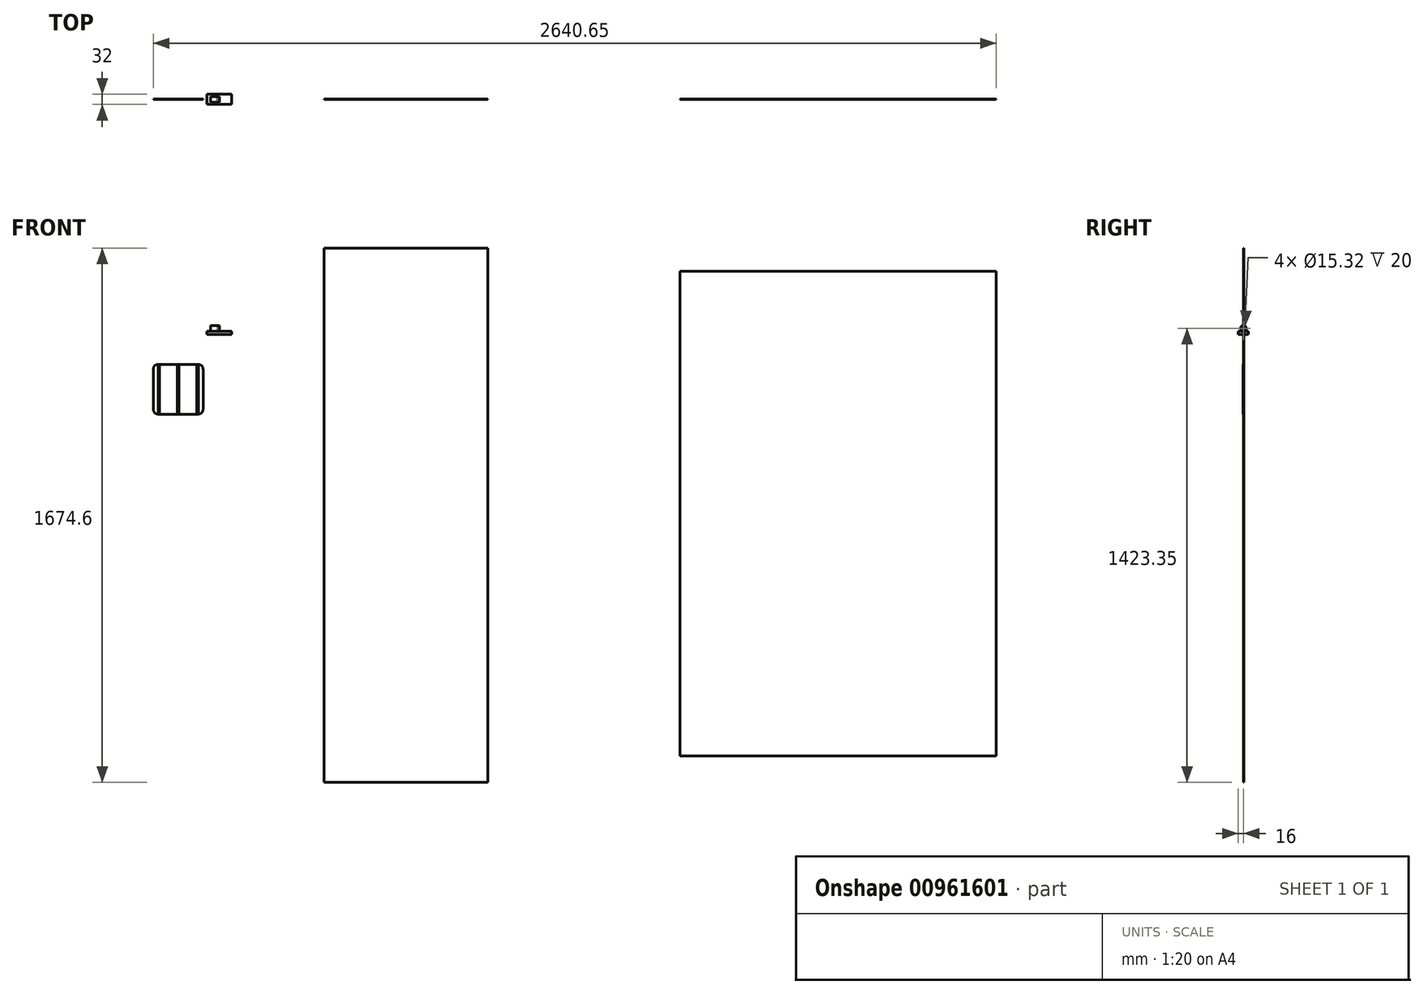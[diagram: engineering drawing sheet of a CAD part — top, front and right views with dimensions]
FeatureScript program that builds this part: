
annotation { "Feature Type Name" : "Feature", "Feature Type Description" : "" }
export const myFeature = defineFeature(function(context is Context, id is Id, definition is map)
    precondition{}
    {
        {
            var Q0;
            Q0=qCreatedBy(makeId("Front.planeOp"),FACE);
            var sketch = newSketch(context, id + "F0", { "sketchPlane" : qUnion([Q0])});
            skLineSegment(sketch, "E0", {"start": v(1286.74, 1046.2) * mm, "end": v(1798.74, 1046.2) * mm});
            skLineSegment(sketch, "E1", {"start": v(1798.74, -628.4) * mm, "end": v(1286.74, -628.4) * mm});
            skLineSegment(sketch, "E2", {"start": v(1286.74, 1046.2) * mm, "end": v(1286.74, -628.4) * mm});
            skLineSegment(sketch, "E3", {"start": v(1798.74, 1046.2) * mm, "end": v(1798.74, -628.4) * mm});
            skSolve(sketch);
        }
        {
            var Q0;
            Q0=makeQuery(id+"F0.imprint","IMPRINT",FACE,{"disambiguationData":[TD([[makeQuery(id+"F0.imprint","IMPRINT",EDGE,{"derivedFrom":sQuery(id+"F0.wireOp",EDGE,"E0")}),-1.0]])]});
            var sketch = newSketch(context, id + "F1", { "sketchPlane" : qUnion([Q0])});
            skLineSegment(sketch, "E4.bottom", {"start": v(766.3, 681.77) * mm, "end": v(892.3, 681.77) * mm});
            skLineSegment(sketch, "E4.top", {"start": v(766.3, 525.77) * mm, "end": v(892.3, 525.77) * mm});
            skLineSegment(sketch, "E4.left", {"start": v(751.3, 666.77) * mm, "end": v(751.3, 540.77) * mm});
            skLineSegment(sketch, "E4.right", {"start": v(907.3, 666.77) * mm, "end": v(907.3, 540.77) * mm});
            skPoint(sketch, "E5.visualSharp", {"position": v(751.3, 681.77) * mm});
            skArc(sketch, "E5.filletArc", {"start": v(766.3, 681.77) * mm, "mid": v(755.7, 677.38) * mm, "end": v(751.3, 666.77) * mm});
            skPoint(sketch, "E6.visualSharp", {"position": v(907.3, 681.77) * mm});
            skArc(sketch, "E6.filletArc", {"start": v(907.3, 666.77) * mm, "mid": v(902.9, 677.38) * mm, "end": v(892.3, 681.77) * mm});
            skPoint(sketch, "E7.visualSharp", {"position": v(907.3, 525.77) * mm});
            skArc(sketch, "E7.filletArc", {"start": v(892.3, 525.77) * mm, "mid": v(902.9, 530.16) * mm, "end": v(907.3, 540.77) * mm});
            skPoint(sketch, "E8.visualSharp", {"position": v(751.3, 525.77) * mm});
            skArc(sketch, "E8.filletArc", {"start": v(751.3, 540.77) * mm, "mid": v(755.7, 530.16) * mm, "end": v(766.3, 525.77) * mm});
            skLineSegment(sketch, "E9.bottom", {"start": v(3038.85, 81858.35) * mm, "end": v(2869.38, 81858.35) * mm});
            skLineSegment(sketch, "E9.top", {"start": v(3038.85, 72650.5) * mm, "end": v(2869.38, 72650.5) * mm});
            skLineSegment(sketch, "E9.left", {"start": v(3038.85, 81858.35) * mm, "end": v(3038.85, 72650.5) * mm});
            skLineSegment(sketch, "E9.right", {"start": v(2869.38, 81858.35) * mm, "end": v(2869.38, 72650.5) * mm});
            skSolve(sketch);
        }
        {
            var Q0;
            Q0=makeQuery(id+"F0.imprint","IMPRINT",FACE,{"disambiguationData":[TD([[makeQuery(id+"F0.imprint","IMPRINT",EDGE,{"derivedFrom":sQuery(id+"F0.wireOp",EDGE,"E0")}),-1.0]])]});
            extrude(context, id + "F2", {"entities" : qUnion([Q0]), "depth" : 1 * mm, "offsetDistance" : 25 * mm});
        }
        {
            var Q0;
            Q0=makeQuery(id+"F1.imprint","IMPRINT",FACE,{"disambiguationData":[TD([[makeQuery(id+"F1.imprint","IMPRINT",EDGE,{"derivedFrom":sQuery(id+"F1.wireOp",EDGE,"E4.bottom")}),-1.0]])]});
            extrude(context, id + "F3", {"entities" : qUnion([Q0]), "depth" : 1 * mm, "offsetDistance" : 25 * mm});
        }
        {
            var Q0;
            Q0=makeQuery(id+"F3.opExtrude","CAP_FACE",FACE,{"disambiguationData":[OSD([sQuery(id+"F1.wireOp",EDGE,"E4.bottom"),sQuery(id+"F1.wireOp",EDGE,"E4.top"),sQuery(id+"F1.wireOp",EDGE,"E4.left"),sQuery(id+"F1.wireOp",EDGE,"E4.right"),sQuery(id+"F1.wireOp",EDGE,"E5.filletArc"),sQuery(id+"F1.wireOp",EDGE,"E6.filletArc"),sQuery(id+"F1.wireOp",EDGE,"E7.filletArc"),sQuery(id+"F1.wireOp",EDGE,"E8.filletArc")])],"isStart":false});
            var sketch = newSketch(context, id + "F4", { "sketchPlane" : qUnion([Q0])});
            skLineSegment(sketch, "E10.bottom", {"start": v(1068.35, 691.33) * mm, "end": v(1072.64, 691.33) * mm});
            skLineSegment(sketch, "E10.top", {"start": v(1068.35, 535.33) * mm, "end": v(1072.64, 535.33) * mm});
            skLineSegment(sketch, "E10.left", {"start": v(1068.35, 691.33) * mm, "end": v(1068.35, 535.33) * mm});
            skLineSegment(sketch, "E10.right", {"start": v(1072.64, 691.33) * mm, "end": v(1072.64, 535.33) * mm});
            skLineSegment(sketch, "E11.bottom", {"start": v(1040.3, 699.13) * mm, "end": v(1044.6, 699.13) * mm});
            skLineSegment(sketch, "E11.top", {"start": v(1040.3, 543.13) * mm, "end": v(1044.6, 543.13) * mm});
            skLineSegment(sketch, "E11.left", {"start": v(1040.3, 699.13) * mm, "end": v(1040.3, 543.13) * mm});
            skLineSegment(sketch, "E11.right", {"start": v(1044.6, 699.13) * mm, "end": v(1044.6, 543.13) * mm});
            skLineSegment(sketch, "E12.bottom", {"start": v(997.94, 678.37) * mm, "end": v(1002.23, 678.37) * mm});
            skLineSegment(sketch, "E12.top", {"start": v(997.94, 522.37) * mm, "end": v(1002.23, 522.37) * mm});
            skLineSegment(sketch, "E12.left", {"start": v(997.94, 678.37) * mm, "end": v(997.94, 522.37) * mm});
            skLineSegment(sketch, "E12.right", {"start": v(1002.23, 678.37) * mm, "end": v(1002.23, 522.37) * mm});
            skSolve(sketch);
        }
        {
            var Q0;
            Q0=makeQuery(id+"F4.imprint","IMPRINT",FACE,{"disambiguationData":[TD([[makeQuery(id+"F4.imprint","IMPRINT",EDGE,{"derivedFrom":sQuery(id+"F4.wireOp",EDGE,"E10.bottom")}),-1.0]])]});
            var Q1;
            Q1=makeQuery(id+"F4.imprint","IMPRINT",FACE,{"disambiguationData":[TD([[makeQuery(id+"F4.imprint","IMPRINT",EDGE,{"derivedFrom":sQuery(id+"F4.wireOp",EDGE,"E11.bottom")}),-1.0]])]});
            var Q2;
            Q2=makeQuery(id+"F4.imprint","IMPRINT",FACE,{"disambiguationData":[TD([[makeQuery(id+"F4.imprint","IMPRINT",EDGE,{"derivedFrom":sQuery(id+"F4.wireOp",EDGE,"E12.bottom")}),-1.0]])]});
            extrude(context, id + "F5", {"entities" : qUnion([Q0, Q1, Q2]), "depth" : 0.5 * mm, "offsetDistance" : 25 * mm});
        }
        {
            var Q0;
            Q0=makeQuery(id+"F5.opExtrude","SWEPT_BODY",BODY,{"disambiguationData":[OSD([sQuery(id+"F4.wireOp",EDGE,"E12.bottom"),sQuery(id+"F4.wireOp",EDGE,"E12.top"),sQuery(id+"F4.wireOp",EDGE,"E12.left"),sQuery(id+"F4.wireOp",EDGE,"E12.right")])]});
            transform(context, id + "F6", {"entities" : qUnion([Q0]), "transformType" : TransformType.TRANSLATION_3D, "dx" : -232.8 * mm, "dy" : 0 * mm, "dz" : 3.3 * mm, "makeCopy" : false});
        }
        {
            var Q0;
            Q0=makeQuery(id+"F5.opExtrude","SWEPT_BODY",BODY,{"disambiguationData":[OSD([sQuery(id+"F4.wireOp",EDGE,"E12.bottom"),sQuery(id+"F4.wireOp",EDGE,"E12.top"),sQuery(id+"F4.wireOp",EDGE,"E12.left"),sQuery(id+"F4.wireOp",EDGE,"E12.right")])]});
            transform(context, id + "F7", {"entities" : qUnion([Q0]), "transformType" : TransformType.TRANSLATION_3D, "dx" : 6E-4000 * mm, "dy" : 0 * mm, "dz" : 0 * mm, "makeCopy" : false});
        }
        {
            var Q0;
            Q0=makeQuery(id+"F5.opExtrude","SWEPT_BODY",BODY,{"disambiguationData":[OSD([sQuery(id+"F4.wireOp",EDGE,"E12.bottom"),sQuery(id+"F4.wireOp",EDGE,"E12.top"),sQuery(id+"F4.wireOp",EDGE,"E12.left"),sQuery(id+"F4.wireOp",EDGE,"E12.right")])]});
            var Q1;
            Q1=makeQuery(id+"F5.opExtrude","CAP_VERTEX",VERTEX,{"disambiguationData":[OSD([sQuery(id+"F4.wireOp",EDGE,"E12.top"),sQuery(id+"F4.wireOp",EDGE,"E12.left")])],"isStart":false});
            var Q2;
            Q2=makeQuery(id+"F3.opExtrude","CAP_EDGE",EDGE,{"disambiguationData":[OSD([sQuery(id+"F1.wireOp",EDGE,"E4.top")])],"isStart":false});
            transform(context, id + "F8", {"entities" : qUnion([Q0]), "transformType" : TransformType.TRANSLATION_ENTITY, "oppositeDirectionEntity" : false, "transformLine" : qUnion([Q1, Q2]), "makeCopy" : false});
        }
        {
            var Q0;
            Q0=makeQuery(id+"F5.opExtrude","SWEPT_BODY",BODY,{"disambiguationData":[OSD([sQuery(id+"F4.wireOp",EDGE,"E12.bottom"),sQuery(id+"F4.wireOp",EDGE,"E12.top"),sQuery(id+"F4.wireOp",EDGE,"E12.left"),sQuery(id+"F4.wireOp",EDGE,"E12.right")])]});
            var Q1;
            Q1=makeQuery(id+"F5.opExtrude","CAP_VERTEX",VERTEX,{"disambiguationData":[OSD([sQuery(id+"F4.wireOp",EDGE,"E12.bottom"),sQuery(id+"F4.wireOp",EDGE,"E12.right")])],"isStart":true});
            var Q2;
            Q2=makeQuery(id+"F3.opExtrude","CAP_VERTEX",VERTEX,{"disambiguationData":[OSD([sQuery(id+"F1.wireOp",EDGE,"E4.bottom"),sQuery(id+"F1.wireOp",EDGE,"E6.filletArc")])],"isStart":false});
            transform(context, id + "F9", {"entities" : qUnion([Q0]), "transformType" : TransformType.TRANSLATION_ENTITY, "oppositeDirectionEntity" : false, "transformLine" : qUnion([Q1, Q2]), "makeCopy" : false});
        }
        {
            var Q0;
            Q0=makeQuery(id+"F5.opExtrude","SWEPT_BODY",BODY,{"disambiguationData":[OSD([sQuery(id+"F4.wireOp",EDGE,"E11.bottom"),sQuery(id+"F4.wireOp",EDGE,"E11.top"),sQuery(id+"F4.wireOp",EDGE,"E11.left"),sQuery(id+"F4.wireOp",EDGE,"E11.right")])]});
            var Q1;
            Q1=sQuery(id+"F4.wireOp",VERTEX,"E11.bottom.start");
            var Q2;
            Q2=makeQuery(id+"F3.opExtrude","CAP_VERTEX",VERTEX,{"disambiguationData":[OSD([sQuery(id+"F1.wireOp",EDGE,"E4.bottom"),sQuery(id+"F1.wireOp",EDGE,"E5.filletArc")])],"isStart":false});
            transform(context, id + "F10", {"entities" : qUnion([Q0]), "transformType" : TransformType.TRANSLATION_ENTITY, "oppositeDirectionEntity" : false, "transformLine" : qUnion([Q1, Q2]), "makeCopy" : false});
        }
        {
            var Q0;
            Q0=sQuery(id+"F4.wireOp",EDGE,"E10.bottom");
            cPoint(context, id + "F11", {"entities" : qUnion([Q0]), "parameter" : 0.5});
        }
        {
            var Q0;
            Q0=makeQuery(id+"F3.opExtrude","CAP_EDGE",EDGE,{"disambiguationData":[OSD([sQuery(id+"F1.wireOp",EDGE,"E4.bottom")])],"isStart":false});
            cPoint(context, id + "F12", {"entities" : qUnion([Q0]), "parameter" : 0.5});
        }
        {
            var Q0;
            Q0=makeQuery(id+"F5.opExtrude","SWEPT_BODY",BODY,{"disambiguationData":[OSD([sQuery(id+"F4.wireOp",EDGE,"E10.bottom"),sQuery(id+"F4.wireOp",EDGE,"E10.top"),sQuery(id+"F4.wireOp",EDGE,"E10.left"),sQuery(id+"F4.wireOp",EDGE,"E10.right")])]});
            var Q1;
            Q1=qCreatedBy(id+"F11",VERTEX);
            var Q2;
            Q2=qCreatedBy(id+"F12",VERTEX);
            transform(context, id + "F13", {"entities" : qUnion([Q0]), "transformType" : TransformType.TRANSLATION_ENTITY, "oppositeDirectionEntity" : false, "transformLine" : qUnion([Q1, Q2]), "makeCopy" : false});
        }
        {
            var Q0;
            Q0=makeQuery(id+"F2.opExtrude","CAP_FACE",FACE,{"disambiguationData":[OSD([sQuery(id+"F0.wireOp",EDGE,"E0"),sQuery(id+"F0.wireOp",EDGE,"E1"),sQuery(id+"F0.wireOp",EDGE,"E2"),sQuery(id+"F0.wireOp",EDGE,"E3")])],"isStart":false});
            var sketch = newSketch(context, id + "F14", { "sketchPlane" : qUnion([Q0])});
            skLineSegment(sketch, "E13.bottom", {"start": v(919.16, 786.05) * mm, "end": v(997.16, 786.05) * mm});
            skLineSegment(sketch, "E13.top", {"start": v(919.16, 776.05) * mm, "end": v(997.16, 776.05) * mm});
            skLineSegment(sketch, "E13.left", {"start": v(919.16, 786.05) * mm, "end": v(919.16, 776.05) * mm});
            skLineSegment(sketch, "E13.right", {"start": v(997.16, 786.05) * mm, "end": v(997.16, 776.05) * mm});
            skPoint(sketch, "E14.oppositeSnap0", {"position": v(958.16, 786.05) * mm});
            skLineSegment(sketch, "E14.bottom", {"start": v(997.16, 786.05) * mm, "end": v(958.16, 786.05) * mm});
            skLineSegment(sketch, "E14.top", {"start": v(997.16, 803.85) * mm, "end": v(958.16, 803.85) * mm});
            skLineSegment(sketch, "E14.left", {"start": v(997.16, 786.05) * mm, "end": v(997.16, 803.85) * mm});
            skLineSegment(sketch, "E14.right", {"start": v(958.16, 786.05) * mm, "end": v(958.16, 803.85) * mm});
            skLineSegment(sketch, "E15.bottom", {"start": v(958.16, 794.95) * mm, "end": v(930.77, 794.95) * mm});
            skLineSegment(sketch, "E15.top", {"start": v(958.16, 786.05) * mm, "end": v(930.77, 786.05) * mm});
            skLineSegment(sketch, "E15.left", {"start": v(958.16, 794.95) * mm, "end": v(958.16, 786.05) * mm});
            skLineSegment(sketch, "E15.right", {"start": v(930.77, 794.95) * mm, "end": v(930.77, 786.05) * mm});
            skSolve(sketch);
        }
        {
            var Q0;
            Q0=makeQuery(id+"F14.imprint","IMPRINT",FACE,{"disambiguationData":[TD([[makeQuery(id+"F14.imprint","IMPRINT",EDGE,{"derivedFrom":sQuery(id+"F14.wireOp",EDGE,"E14.bottom")}),-1.0]])]});
            var Q1;
            Q1=makeQuery(id+"F14.imprint","IMPRINT",FACE,{"disambiguationData":[TD([[makeQuery(id+"F14.imprint","IMPRINT",EDGE,{"derivedFrom":sQuery(id+"F14.wireOp",EDGE,"E13.bottom")}),-1.0]])]});
            extrude(context, id + "F15", {"entities" : qUnion([Q0, Q1]), "endBound" : BoundingType.SYMMETRIC, "depth" : 32 * mm, "offsetDistance" : 25 * mm});
        }
        {
            var Q0;
            Q0=makeQuery(id+"F14.imprint","IMPRINT",FACE,{"disambiguationData":[TD([[makeQuery(id+"F14.imprint","IMPRINT",EDGE,{"derivedFrom":sQuery(id+"F14.wireOp",EDGE,"E15.bottom")}),1.0]])]});
            var Q1;
            Q1=sQuery(id+"F14.wireOp",EDGE,"E15.bottom");
            revolve(context, id + "F16", {"surfaceOperationType" : NewSurfaceOperationType.NEW, "entities" : qUnion([Q0]), "axis" : qUnion([Q1]), "revolveType" : RevolveType.ONE_DIRECTION, "angle" : 360 * degree});
        }
        {
            var Q0;
            Q0=makeQuery(id+"F16.opRevolve","SWEPT_FACE",FACE,{"disambiguationData":[OSD([sQuery(id+"F14.wireOp",EDGE,"E15.right")])]});
            var sketch = newSketch(context, id + "F17", { "sketchPlane" : qUnion([Q0])});
            skCircle(sketch, "E16", {"center": v(1, 794.95) * mm, "radius": 7.66 * mm});
            skSolve(sketch);
        }
        {
            var Q0;
            Q0=makeQuery(id+"F17.imprint","IMPRINT",FACE,{"disambiguationData":[TD([[makeQuery(id+"F17.imprint","IMPRINT",EDGE,{"derivedFrom":sQuery(id+"F17.wireOp",EDGE,"E16")}),1.0]])]});
            extrude(context, id + "F18", {"entities" : qUnion([Q0]), "operationType" : NewBodyOperationType.REMOVE, "depth" : -20 * mm, "offsetDistance" : 25 * mm});
        }
        {
            var Q0;
            Q0=qCreatedBy(makeId("Front.planeOp"),FACE);
            var sketch = newSketch(context, id + "F19", { "sketchPlane" : qUnion([Q0])});
            skLineSegment(sketch, "E17.bottom", {"start": v(2401.95, 973.5) * mm, "end": v(3391.95, 973.5) * mm});
            skLineSegment(sketch, "E17.top", {"start": v(2401.95, -545.5) * mm, "end": v(3391.95, -545.5) * mm});
            skLineSegment(sketch, "E17.left", {"start": v(2401.95, 973.5) * mm, "end": v(2401.95, -545.5) * mm});
            skLineSegment(sketch, "E17.right", {"start": v(3391.95, 973.5) * mm, "end": v(3391.95, -545.5) * mm});
            skSolve(sketch);
        }
        {
            var Q0;
            Q0=makeQuery(id+"F19.imprint","IMPRINT",FACE,{"disambiguationData":[TD([[makeQuery(id+"F19.imprint","IMPRINT",EDGE,{"derivedFrom":sQuery(id+"F19.wireOp",EDGE,"E17.bottom")}),-1.0]])]});
            extrude(context, id + "F20", {"entities" : qUnion([Q0]), "depth" : 1 * mm, "offsetDistance" : 25 * mm});
        }
    });
